# Revit family: Hager-Univers-IP44-syst-Surface_mounted-NoHosted-UK-en
name_source: partatom
category: Electrical Equipment
units: mm (PartAtom-declared; Revit-internal decimal feet)

## family parameters
Always vertical = Yes
Cut with Voids When Loaded = No
Panel Configuration = Two Columns, Circuits Across
Part Type = Panelboard
Room Calculation Point = No
Round Connector Dimension = Use Diameter
Shared = No
Work Plane-Based = Yes

## types (8) — shared parameters
Default Elevation = 1219 mm
EF000003 - Mounting method = EV001247 - Surface mounted/recessed mounted
EF000007 - Colour = EV000202 - White
EF000049 - Depth = 161 mm  [stored 0.528215 ft]
EF000116 - RAL-number = 9010
EF000118 - With mounting plate = No
EF000218 - Built-in depth = 161 mm  [stored 0.528215 ft]
EF000339 - Type of cover = EV004216 - Door
EF001062 - EMC-version = No
EF001088 - Extension possible = Yes
EF001131 - Internal depth = 161 mm  [stored 0.528215 ft]
EF001134 - DIN-rail = Yes
EF001596 - Material housing = EV000179 - Steel
EF002950 - Width in number of modular spacings = 12
EF004462 - Type of closure = EV000154 - Other
EF005474 - Degree of protection (IP) = EV006418 - IP44
EF006244 - Transparent cover/door = No
EF006306 - With lock = No
EF009212 - Cover model = EV009916 - With notch
EF015776 - Earthing terminal block = No
EF015941 - Signal passing door = No
HG000002 - With door or cover = Yes
HG000003 - Range = Univers
HG000005 - Thickness = 3 mm  [stored 0.00984252 ft]
HG000006 - Flush mounted = No
HG000011 - Empty rows from bottom = No
HG000017 - Distance between poles = 18 mm  [stored 0.0590551 ft]
Manufacturer = Hager
Type Comments = Univers
zero-valued in all types: HG000007 - Number of empty columns, HG000008 - Number of empty rows

## per-type parameters (varying)
| type | EF000008 - Width | EF000040 - Height | EF000266 - Number of rows | EF000332 - Built-in height | EF000846 - Built-in width | EF015777 - Neutral terminal block | HG000001 - Number of columns | HG000004 - Manufacturer reference | HG000009 - Double swing door | HG000010 - Asymmetric doors | Model |
| Surface mounted IP44 W1050 H1100 D161 12 Modular spacings - FWB74 | 1050 mm | 1100 mm  [stored 3.60892 ft] | 28 | 1100 mm  [stored 3.60892 ft] | 1050 mm | Yes | 4 | FWB74 | Yes | No | FWB74 |
| Surface mounted IP44 W1050 H1100 D161 12 Modular spacings - FWB74S | 1050 mm | 1100 mm  [stored 3.60892 ft] | 28 | 1100 mm  [stored 3.60892 ft] | 1050 mm | No | 4 | FWB74S | Yes | No | FWB74S |
| Surface mounted IP44 W550 H1100 D161 12 Modular spacings - FWB72 | 550 mm | 1100 mm  [stored 3.60892 ft] | 14 | 1100 mm  [stored 3.60892 ft] | 550 mm | Yes | 2 | FWB72 | No | No | FWB72 |
| Surface mounted IP44 W550 H1100 D161 12 Modular spacings - FWB72S | 550 mm | 1100 mm  [stored 3.60892 ft] | 14 | 1100 mm  [stored 3.60892 ft] | 550 mm | No | 2 | FWB72S | No | No | FWB72S |
| Surface mounted IP44 W550 H650 D161 12 Modular spacings - FWB42 | 550 mm | 650 mm | 8 | 650 mm | 550 mm | Yes | 2 | FWB42 | No | No | FWB42 |
| Surface mounted IP44 W550 H650 D161 12 Modular spacings - FWB42S | 550 mm | 650 mm | 8 | 650 mm | 550 mm | No | 2 | FWB42S | No | No | FWB42S |
| Surface mounted IP44 W800 H1100 D161 12 Modular spacings - FWB73 | 800 mm  [stored 2.62467 ft] | 1100 mm  [stored 3.60892 ft] | 21 | 1100 mm  [stored 3.60892 ft] | 800 mm  [stored 2.62467 ft] | Yes | 3 | FWB73 | Yes | Yes | FWB73 |
| Surface mounted IP44 W800 H1100 D161 12 Modular spacings - FWB73S | 800 mm  [stored 2.62467 ft] | 1100 mm  [stored 3.60892 ft] | 21 | 1100 mm  [stored 3.60892 ft] | 800 mm  [stored 2.62467 ft] | No | 3 | FWB73S | Yes | Yes | FWB73S |

note: [stored X ft] marks values corroborated as IEEE doubles in the binary element streams (Revit-internal decimal feet)

## geometry (parser evidence)
native form markers: Sweep x14
no freeform markers — native parametric forms only
